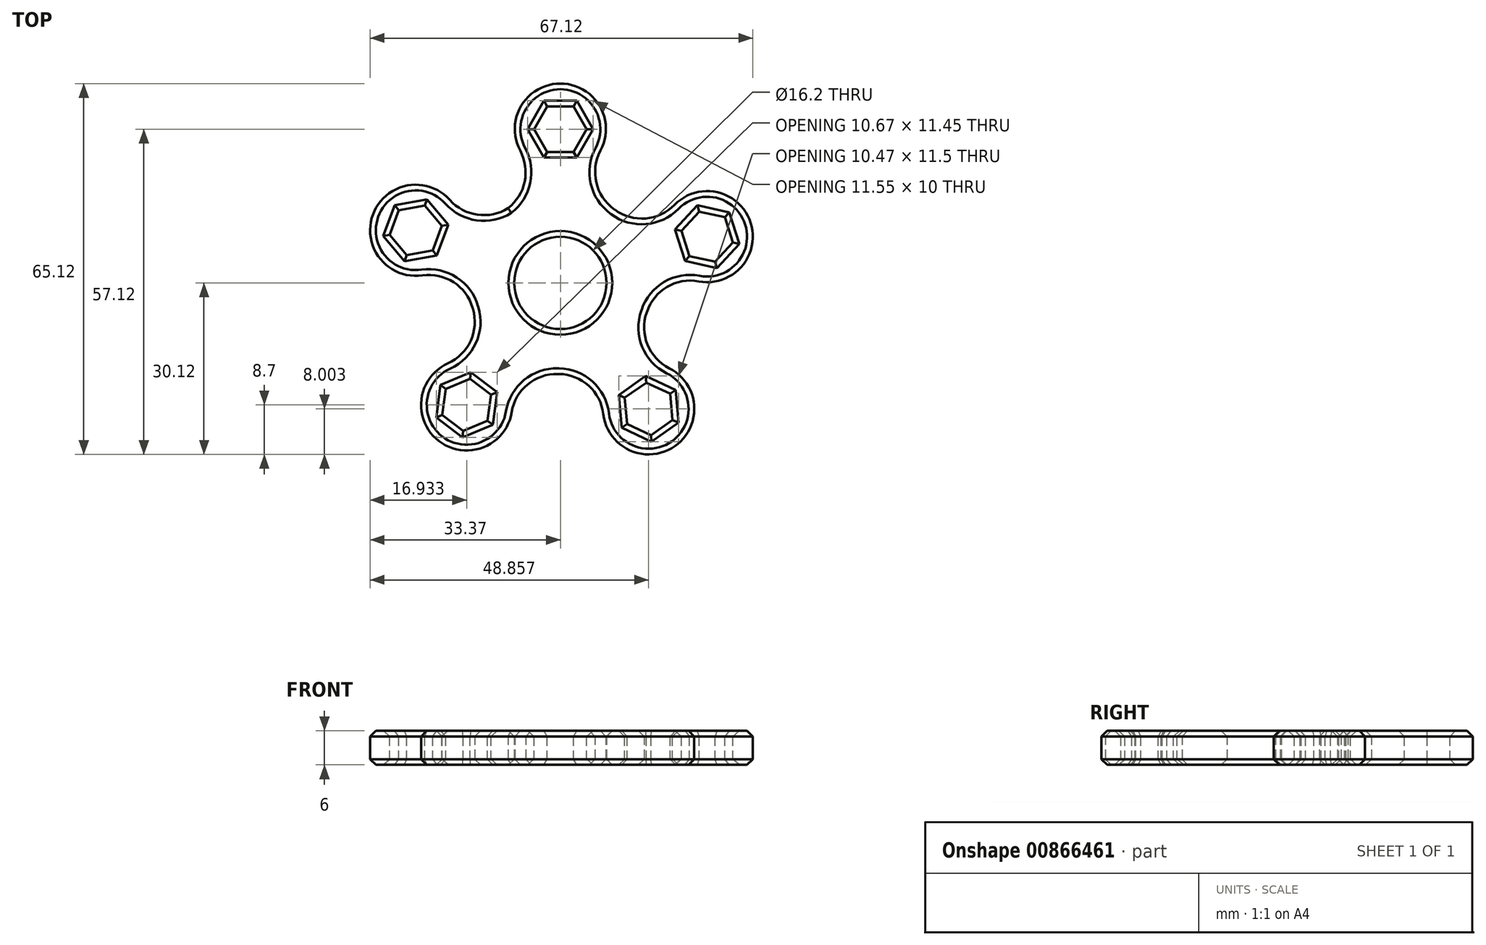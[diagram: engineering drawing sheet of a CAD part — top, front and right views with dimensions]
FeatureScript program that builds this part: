
annotation { "Feature Type Name" : "Feature", "Feature Type Description" : "" }
export const myFeature = defineFeature(function(context is Context, id is Id, definition is map)
    precondition{}
    {
        {
            var Q0;
            Q0=qCreatedBy(makeId("Top.planeOp"),FACE);
            var sketch = newSketch(context, id + "F0", { "sketchPlane" : qUnion([Q0])});
            skCircle(sketch, "E0", {"center": v(0, 0) * mm, "radius": 35 * mm, "construction": true});
            skCircle(sketch, "E1", {"center": v(0, 0) * mm, "radius": 16 * mm});
            skCircle(sketch, "E2", {"center": v(0, 0) * mm, "radius": 8.1 * mm});
            skCircle(sketch, "E3", {"center": v(0, 27) * mm, "radius": 8 * mm});
            skArc(sketch, "E4", {"start": v(-9.4, 12.95) * mm, "mid": v(-6.3, 17.64) * mm, "end": v(-7.05, 23.21) * mm});
            skArc(sketch, "E5.MirrorCS", {"start": v(9.4, 12.95) * mm, "mid": v(6.3, 17.64) * mm, "end": v(7.05, 23.21) * mm});
            skCircle(sketch, "E6.1.0", {"center": v(25.75, 8.12) * mm, "radius": 8 * mm});
            skArc(sketch, "E6.1.1", {"start": v(15.18, -5.07) * mm, "mid": v(18.72, -0.7) * mm, "end": v(24.26, 0.26) * mm});
            skArc(sketch, "E6.1.2", {"start": v(9.53, 12.86) * mm, "mid": v(14.93, 11.3) * mm, "end": v(20.02, 13.7) * mm});
            skCircle(sketch, "E6.2.0", {"center": v(15.49, -22.12) * mm, "radius": 8 * mm});
            skArc(sketch, "E6.2.1", {"start": v(-0.27, -16) * mm, "mid": v(4.96, -18.06) * mm, "end": v(7.54, -23.06) * mm});
            skArc(sketch, "E6.2.2", {"start": v(15.12, -5.22) * mm, "mid": v(15.28, -10.84) * mm, "end": v(19.09, -14.97) * mm});
            skCircle(sketch, "E6.3.0", {"center": v(-16.44, -21.42) * mm, "radius": 8 * mm});
            skArc(sketch, "E6.3.1", {"start": v(-15.34, -4.55) * mm, "mid": v(-15.73, -10.16) * mm, "end": v(-19.72, -14.13) * mm});
            skArc(sketch, "E6.3.2", {"start": v(-0.43, -16) * mm, "mid": v(-5.74, -17.83) * mm, "end": v(-8.54, -22.7) * mm});
            skCircle(sketch, "E6.4.0", {"center": v(-25.37, 9.23) * mm, "radius": 8 * mm});
            skArc(sketch, "E6.4.1", {"start": v(-8.96, 13.26) * mm, "mid": v(-14.42, 11.95) * mm, "end": v(-19.4, 14.56) * mm});
            skArc(sketch, "E6.4.2", {"start": v(-15.38, -4.4) * mm, "mid": v(-18.73, 0.12) * mm, "end": v(-24.22, 1.32) * mm});
            skLineSegment(sketch, "E6.anchor1", {"start": v(0, 0) * mm, "end": v(-9.4, 12.95) * mm, "construction": true});
            skLineSegment(sketch, "E6.anchor2", {"start": v(0, 0) * mm, "end": v(-15.38, -4.4) * mm, "construction": true});
            skLineSegment(sketch, "E7", {"start": v(25.75, 8.12) * mm, "end": v(0, 0) * mm, "construction": true});
            skLineSegment(sketch, "E8", {"start": v(15.49, -22.12) * mm, "end": v(0, 0) * mm, "construction": true});
            skLineSegment(sketch, "E9", {"start": v(-16.44, -21.42) * mm, "end": v(0, 0) * mm, "construction": true});
            skLineSegment(sketch, "E10", {"start": v(-25.37, 9.23) * mm, "end": v(0, 0) * mm, "construction": true});
            skLineSegment(sketch, "E11", {"start": v(0, 27) * mm, "end": v(0, 0) * mm, "construction": true});
            skSolve(sketch);
        }
        {
            var Q0;
            Q0 = qSketchRegion(id + "F0", true);
            extrude(context, id + "F1", {"entities" : qUnion([Q0]), "depth" : 6 * mm, "offsetDistance" : 25 * mm});
        }
        {
            var Q0;
            Q0=makeQuery(id+"F1.opExtrude","CAP_FACE",FACE,{"disambiguationData":[OSD([sQuery(id+"F0.wireOp",EDGE,"E1"),sQuery(id+"F0.wireOp",EDGE,"E2"),sQuery(id+"F0.wireOp",EDGE,"E3"),sQuery(id+"F0.wireOp",EDGE,"E4"),sQuery(id+"F0.wireOp",EDGE,"E5.MirrorCS"),sQuery(id+"F0.wireOp",EDGE,"E6.1.0"),sQuery(id+"F0.wireOp",EDGE,"E6.1.1"),sQuery(id+"F0.wireOp",EDGE,"E6.1.2"),sQuery(id+"F0.wireOp",EDGE,"E6.2.0"),sQuery(id+"F0.wireOp",EDGE,"E6.2.1"),sQuery(id+"F0.wireOp",EDGE,"E6.2.2"),sQuery(id+"F0.wireOp",EDGE,"E6.3.0"),sQuery(id+"F0.wireOp",EDGE,"E6.3.1"),sQuery(id+"F0.wireOp",EDGE,"E6.3.2"),sQuery(id+"F0.wireOp",EDGE,"E6.4.0"),sQuery(id+"F0.wireOp",EDGE,"E6.4.1"),sQuery(id+"F0.wireOp",EDGE,"E6.4.2")])],"isStart":false});
            var sketch = newSketch(context, id + "F2", { "sketchPlane" : qUnion([Q0])});
            skCircle(sketch, "E12.cCircle", {"center": v(0, 27) * mm, "radius": 4 * mm, "construction": true});
            skLineSegment(sketch, "E12.0", {"start": v(-2.3, 31) * mm, "end": v(2.3, 31) * mm});
            skLineSegment(sketch, "E12.1", {"start": v(2.3, 31) * mm, "end": v(4.62, 27) * mm});
            skLineSegment(sketch, "E12.2", {"start": v(4.62, 27) * mm, "end": v(2.3, 23) * mm});
            skLineSegment(sketch, "E12.3", {"start": v(2.3, 23) * mm, "end": v(-2.3, 23) * mm});
            skLineSegment(sketch, "E12.4", {"start": v(-2.3, 23) * mm, "end": v(-4.62, 27) * mm});
            skLineSegment(sketch, "E12.5", {"start": v(-4.62, 27) * mm, "end": v(-2.3, 31) * mm});
            skPoint(sketch, "E12.0.midPoint", {"position": v(0, 31) * mm});
            skLineSegment(sketch, "E13.0", {"start": v(25.75, 8.12) * mm, "end": v(0, 0) * mm, "construction": true});
            skLineSegment(sketch, "E14.0", {"start": v(15.49, -22.12) * mm, "end": v(0, 0) * mm, "construction": true});
            skLineSegment(sketch, "E15.0", {"start": v(-16.44, -21.42) * mm, "end": v(0, 0) * mm, "construction": true});
            skLineSegment(sketch, "E16.0", {"start": v(-25.37, 9.23) * mm, "end": v(0, 0) * mm, "construction": true});
            skLineSegment(sketch, "E17.0", {"start": v(0, 27) * mm, "end": v(0, 0) * mm, "construction": true});
            skCircle(sketch, "E18.cCircle", {"center": v(25.75, 8.12) * mm, "radius": 4 * mm, "construction": true});
            skLineSegment(sketch, "E18.0", {"start": v(22.63, 4.71) * mm, "end": v(21.24, 9.12) * mm});
            skLineSegment(sketch, "E18.1", {"start": v(21.24, 9.12) * mm, "end": v(24.36, 12.52) * mm});
            skLineSegment(sketch, "E18.2", {"start": v(24.36, 12.52) * mm, "end": v(28.87, 11.52) * mm});
            skLineSegment(sketch, "E18.3", {"start": v(28.87, 11.52) * mm, "end": v(30.26, 7.12) * mm});
            skLineSegment(sketch, "E18.4", {"start": v(30.26, 7.12) * mm, "end": v(27.14, 3.71) * mm});
            skLineSegment(sketch, "E18.5", {"start": v(27.14, 3.71) * mm, "end": v(22.63, 4.71) * mm});
            skPoint(sketch, "E18.0.midPoint", {"position": v(21.94, 6.92) * mm});
            skCircle(sketch, "E19.cCircle", {"center": v(15.49, -22.12) * mm, "radius": 4 * mm, "construction": true});
            skLineSegment(sketch, "E19.0", {"start": v(11.3, -20.17) * mm, "end": v(15.08, -17.52) * mm});
            skLineSegment(sketch, "E19.1", {"start": v(15.08, -17.52) * mm, "end": v(19.27, -19.47) * mm});
            skLineSegment(sketch, "E19.2", {"start": v(19.27, -19.47) * mm, "end": v(19.67, -24.07) * mm});
            skLineSegment(sketch, "E19.3", {"start": v(19.67, -24.07) * mm, "end": v(15.89, -26.72) * mm});
            skLineSegment(sketch, "E19.4", {"start": v(15.89, -26.72) * mm, "end": v(11.7, -24.77) * mm});
            skLineSegment(sketch, "E19.5", {"start": v(11.7, -24.77) * mm, "end": v(11.3, -20.17) * mm});
            skPoint(sketch, "E19.0.midPoint", {"position": v(13.2, -18.84) * mm});
            skCircle(sketch, "E20.cCircle", {"center": v(-25.37, 9.23) * mm, "radius": 4 * mm, "construction": true});
            skLineSegment(sketch, "E20.0", {"start": v(-20.82, 10.04) * mm, "end": v(-22.4, 5.7) * mm});
            skLineSegment(sketch, "E20.1", {"start": v(-22.4, 5.7) * mm, "end": v(-26.95, 4.9) * mm});
            skLineSegment(sketch, "E20.2", {"start": v(-26.95, 4.9) * mm, "end": v(-29.92, 8.43) * mm});
            skLineSegment(sketch, "E20.3", {"start": v(-29.92, 8.43) * mm, "end": v(-28.34, 12.77) * mm});
            skLineSegment(sketch, "E20.4", {"start": v(-28.34, 12.77) * mm, "end": v(-23.8, 13.57) * mm});
            skLineSegment(sketch, "E20.5", {"start": v(-23.8, 13.57) * mm, "end": v(-20.82, 10.04) * mm});
            skPoint(sketch, "E20.0.midPoint", {"position": v(-21.61, 7.87) * mm});
            skCircle(sketch, "E21.cCircle", {"center": v(-16.44, -21.42) * mm, "radius": 4 * mm, "construction": true});
            skLineSegment(sketch, "E21.0", {"start": v(-15.83, -16.84) * mm, "end": v(-12.17, -19.65) * mm});
            skLineSegment(sketch, "E21.1", {"start": v(-12.17, -19.65) * mm, "end": v(-12.77, -24.23) * mm});
            skLineSegment(sketch, "E21.2", {"start": v(-12.77, -24.23) * mm, "end": v(-17.04, -26) * mm});
            skLineSegment(sketch, "E21.3", {"start": v(-17.04, -26) * mm, "end": v(-20.7, -23.19) * mm});
            skLineSegment(sketch, "E21.4", {"start": v(-20.7, -23.19) * mm, "end": v(-20.1, -18.6) * mm});
            skLineSegment(sketch, "E21.5", {"start": v(-20.1, -18.6) * mm, "end": v(-15.83, -16.84) * mm});
            skPoint(sketch, "E21.0.midPoint", {"position": v(-14, -18.25) * mm});
            skSolve(sketch);
        }
        {
            var Q0;
            Q0 = qSketchRegion(id + "F2", true);
            extrude(context, id + "F3", {"entities" : qUnion([Q0]), "operationType" : NewBodyOperationType.REMOVE, "oppositeDirection" : true, "depth" : 25 * mm, "offsetDistance" : 25 * mm});
        }
        {
            var Q0;
            Q0=makeQuery(id+"F1.opExtrude","CAP_FACE",FACE,{"disambiguationData":[OSD([sQuery(id+"F0.wireOp",EDGE,"E1"),sQuery(id+"F0.wireOp",EDGE,"E2"),sQuery(id+"F0.wireOp",EDGE,"E3"),sQuery(id+"F0.wireOp",EDGE,"E4"),sQuery(id+"F0.wireOp",EDGE,"E5.MirrorCS"),sQuery(id+"F0.wireOp",EDGE,"E6.1.0"),sQuery(id+"F0.wireOp",EDGE,"E6.1.1"),sQuery(id+"F0.wireOp",EDGE,"E6.1.2"),sQuery(id+"F0.wireOp",EDGE,"E6.2.0"),sQuery(id+"F0.wireOp",EDGE,"E6.2.1"),sQuery(id+"F0.wireOp",EDGE,"E6.2.2"),sQuery(id+"F0.wireOp",EDGE,"E6.3.0"),sQuery(id+"F0.wireOp",EDGE,"E6.3.1"),sQuery(id+"F0.wireOp",EDGE,"E6.3.2"),sQuery(id+"F0.wireOp",EDGE,"E6.4.0"),sQuery(id+"F0.wireOp",EDGE,"E6.4.1"),sQuery(id+"F0.wireOp",EDGE,"E6.4.2")])],"isStart":false});
            var Q1;
            Q1=makeQuery(id+"F1.opExtrude","CAP_FACE",FACE,{"disambiguationData":[OSD([sQuery(id+"F0.wireOp",EDGE,"E1"),sQuery(id+"F0.wireOp",EDGE,"E2"),sQuery(id+"F0.wireOp",EDGE,"E3"),sQuery(id+"F0.wireOp",EDGE,"E4"),sQuery(id+"F0.wireOp",EDGE,"E5.MirrorCS"),sQuery(id+"F0.wireOp",EDGE,"E6.1.0"),sQuery(id+"F0.wireOp",EDGE,"E6.1.1"),sQuery(id+"F0.wireOp",EDGE,"E6.1.2"),sQuery(id+"F0.wireOp",EDGE,"E6.2.0"),sQuery(id+"F0.wireOp",EDGE,"E6.2.1"),sQuery(id+"F0.wireOp",EDGE,"E6.2.2"),sQuery(id+"F0.wireOp",EDGE,"E6.3.0"),sQuery(id+"F0.wireOp",EDGE,"E6.3.1"),sQuery(id+"F0.wireOp",EDGE,"E6.3.2"),sQuery(id+"F0.wireOp",EDGE,"E6.4.0"),sQuery(id+"F0.wireOp",EDGE,"E6.4.1"),sQuery(id+"F0.wireOp",EDGE,"E6.4.2")])],"isStart":true});
            chamfer(context, id + "F4", {"entities" : qUnion([Q0, Q1]), "width" : 1 * mm, "tangentPropagation" : true});
        }
    });
